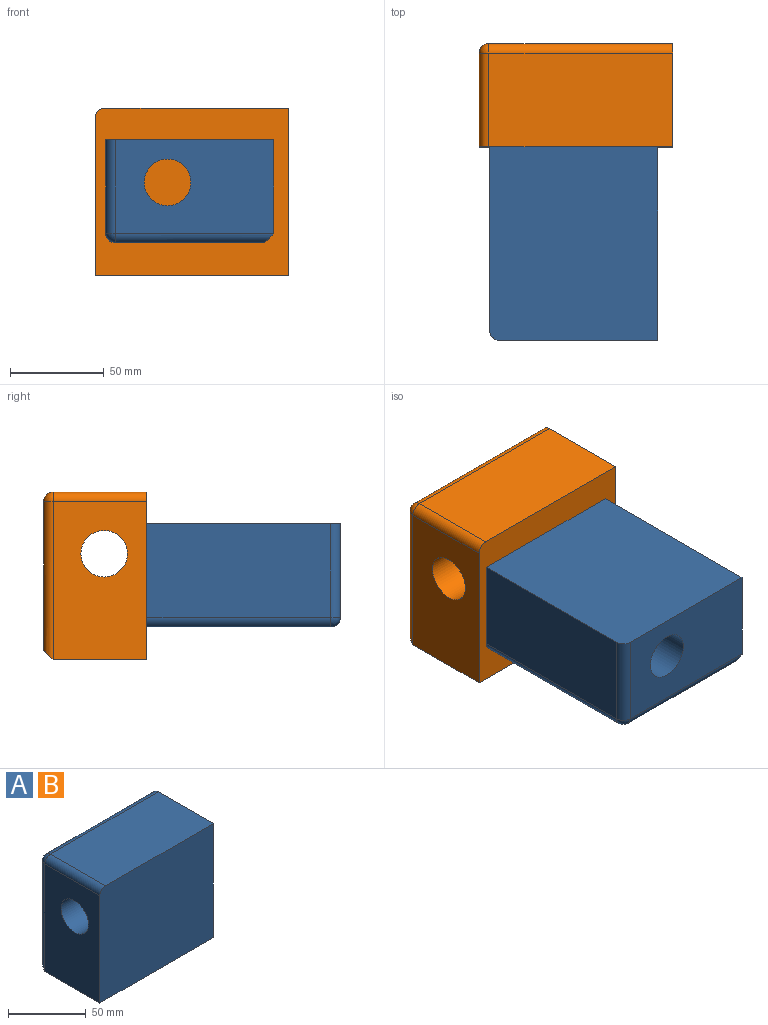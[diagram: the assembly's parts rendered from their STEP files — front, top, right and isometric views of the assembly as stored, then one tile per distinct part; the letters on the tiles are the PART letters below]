
ASSEMBLY  parts=2 mates=1
PART A: 12 faces, bbox 103x55x89.4 mm
  f0: plane 97.93x49.92mm, normal (0,0,1), area 4888.9mm2, adj f3,f4,f9,f11
  f1: plane 84.34x49.92mm, normal (-1,0,0), area 3726.7mm2, adj f2,f4,f6,f8,f11
  f2: plane 103.01x50mm, normal (0,0,-1), area 5150.7mm2, adj f1,f3,f4,f7,f8
  f3: plane 89.42x55mm, normal (1,0,0), area 4416.5mm2, adj f0,f2,f4,f5,f6,f7,f9
  f4: plane 103.01x89.42mm, normal (0,-1,0), area 9206.1mm2, adj f0,f1,f2,f3,f11
  f5: plane 97.93x79.34mm, normal (0,1,0), area 7770.2mm2, adj f3,f7,f8,f9
  f6: cylinder r=12.41mm len=103.01mm, axis (1,0,0), area 8030.4mm2, adj f1,f3
  f7: plane 103.01x5mm, normal (0,0.71,-0.71), area 720.6mm2, adj f2,f3,f5,f8
  f8: cylinder r=5.08mm len=84.34mm, axis (0,0,-1), area 647.8mm2, adj f1,f2,f5,f7,f10
  f9: cylinder r=5.08mm len=97.93mm, axis (-1,0,0), area 781.5mm2, adj f0,f3,f5,f10
  f10: sphere r=5.08mm, area 40.5mm2, adj f8,f9,f11
  f11: cylinder r=5.08mm len=49.92mm, axis (0,-1,0), area 398.3mm2, adj f0,f1,f4,f10
PART B: same geometry as A
PLACE A rot(axis=(-0.58,-0.58,0.58),120deg) t=(46.56,-61.09,-39.65)mm
PLACE B t=(44.97,44.67,-16.08)mm
MATE fastened A.f3 <-> B.f4  axis (0,1,0) through (44.26,-10.33,-12.57)mm
